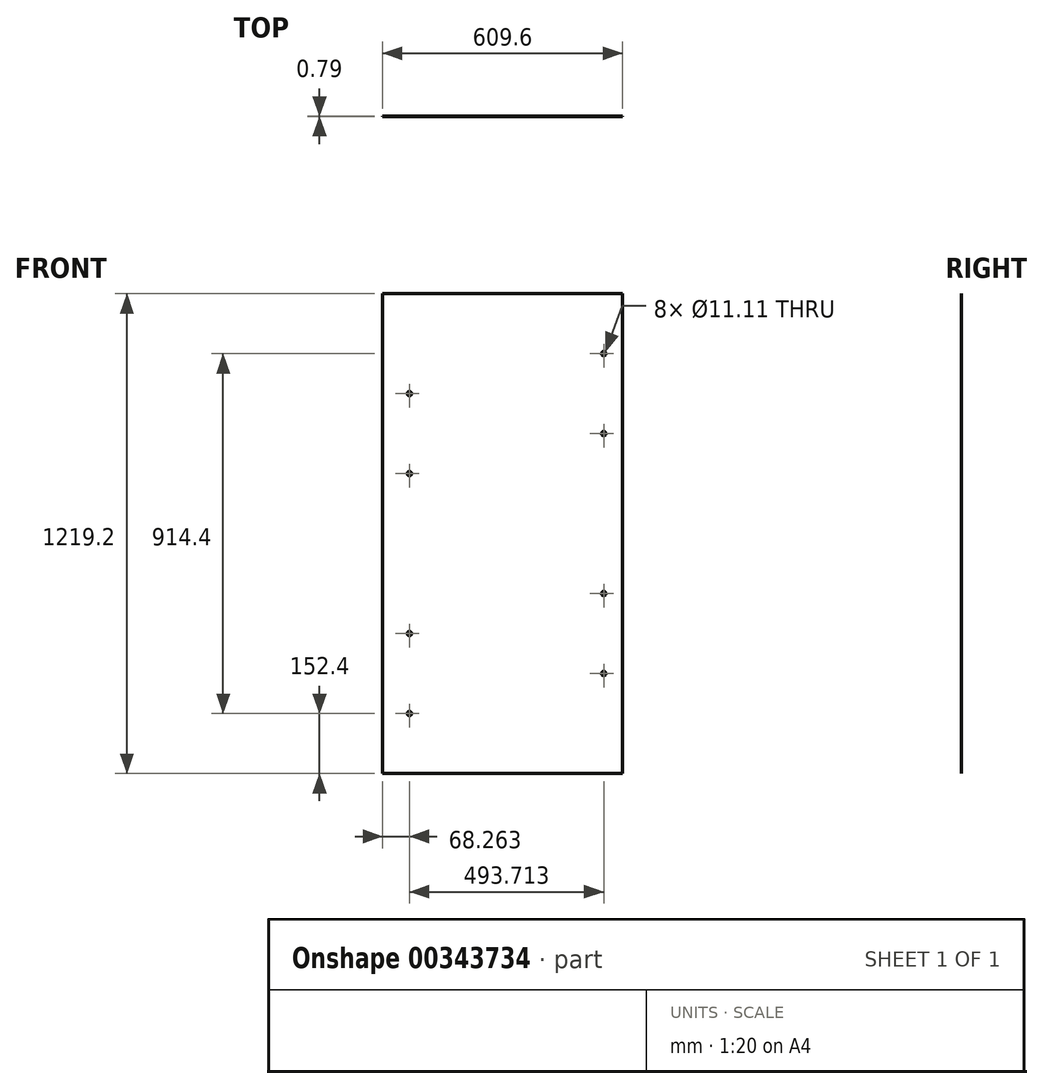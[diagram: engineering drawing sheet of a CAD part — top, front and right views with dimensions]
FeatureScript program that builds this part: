
annotation { "Feature Type Name" : "Feature", "Feature Type Description" : "" }
export const myFeature = defineFeature(function(context is Context, id is Id, definition is map)
    precondition{}
    {
        {
            var Q0;
            Q0=qCreatedBy(makeId("Front.planeOp"),FACE);
            var sketch = newSketch(context, id + "F0", { "sketchPlane" : qUnion([Q0])});
            skLineSegment(sketch, "E0.bottom", {"start": v(0, 0) * mm, "end": v(609.6, 0) * mm});
            skLineSegment(sketch, "E0.top", {"start": v(0, 1219.2) * mm, "end": v(609.6, 1219.2) * mm});
            skLineSegment(sketch, "E0.left", {"start": v(0, 0) * mm, "end": v(0, 1219.2) * mm});
            skLineSegment(sketch, "E0.right", {"start": v(609.6, 0) * mm, "end": v(609.6, 1219.2) * mm});
            skSolve(sketch);
        }
        {
            var Q0;
            Q0=makeQuery(id+"F0.imprint","IMPRINT",FACE,{"disambiguationData":[TD([[makeQuery(id+"F0.imprint","IMPRINT",EDGE,{"derivedFrom":sQuery(id+"F0.wireOp",EDGE,"E0.bottom")}),1.0]])]});
            extrude(context, id + "F1", {"entities" : qUnion([Q0]), "depth" : 0.8 * mm});
        }
        {
            var Q0;
            Q0=makeQuery(id+"F1.opExtrude","CAP_FACE",FACE,{"disambiguationData":[OSD([sQuery(id+"F0.wireOp",EDGE,"E0.bottom"),sQuery(id+"F0.wireOp",EDGE,"E0.top"),sQuery(id+"F0.wireOp",EDGE,"E0.left"),sQuery(id+"F0.wireOp",EDGE,"E0.right")])],"isStart":false});
            var sketch = newSketch(context, id + "F2", { "sketchPlane" : qUnion([Q0])});
            skCircle(sketch, "E1", {"center": v(68.26, 152.4) * mm, "radius": 5.56 * mm});
            skCircle(sketch, "E2", {"center": v(68.26, 355.6) * mm, "radius": 5.56 * mm});
            skCircle(sketch, "E3", {"center": v(561.97, 1066.8) * mm, "radius": 5.56 * mm});
            skCircle(sketch, "E4", {"center": v(561.97, 863.6) * mm, "radius": 5.56 * mm});
            skLineSegment(sketch, "E5", {"start": v(0, 609.6) * mm, "end": v(609.6, 609.6) * mm, "construction": true});
            skCircle(sketch, "E6", {"center": v(68.26, 762) * mm, "radius": 5.56 * mm});
            skCircle(sketch, "E7", {"center": v(68.26, 965.2) * mm, "radius": 5.56 * mm});
            skCircle(sketch, "E8", {"center": v(561.97, 457.2) * mm, "radius": 5.56 * mm});
            skCircle(sketch, "E9", {"center": v(561.97, 254) * mm, "radius": 5.56 * mm});
            skSolve(sketch);
        }
        {
            var Q0;
            Q0=makeQuery(id+"F2.imprint","IMPRINT",FACE,{"disambiguationData":[TD([[makeQuery(id+"F2.imprint","IMPRINT",EDGE,{"derivedFrom":sQuery(id+"F2.wireOp",EDGE,"E1")}),1.0]])]});
            var Q1;
            Q1=makeQuery(id+"F2.imprint","IMPRINT",FACE,{"disambiguationData":[TD([[makeQuery(id+"F2.imprint","IMPRINT",EDGE,{"derivedFrom":sQuery(id+"F2.wireOp",EDGE,"E2")}),1.0]])]});
            var Q2;
            Q2=makeQuery(id+"F2.imprint","IMPRINT",FACE,{"disambiguationData":[TD([[makeQuery(id+"F2.imprint","IMPRINT",EDGE,{"derivedFrom":sQuery(id+"F2.wireOp",EDGE,"E4")}),1.0]])]});
            var Q3;
            Q3=makeQuery(id+"F2.imprint","IMPRINT",FACE,{"disambiguationData":[TD([[makeQuery(id+"F2.imprint","IMPRINT",EDGE,{"derivedFrom":sQuery(id+"F2.wireOp",EDGE,"E3")}),1.0]])]});
            var Q4;
            Q4=makeQuery(id+"F2.imprint","IMPRINT",FACE,{"disambiguationData":[TD([[makeQuery(id+"F2.imprint","IMPRINT",EDGE,{"derivedFrom":sQuery(id+"F2.wireOp",EDGE,"E6")}),1.0]])]});
            var Q5;
            Q5=makeQuery(id+"F2.imprint","IMPRINT",FACE,{"disambiguationData":[TD([[makeQuery(id+"F2.imprint","IMPRINT",EDGE,{"derivedFrom":sQuery(id+"F2.wireOp",EDGE,"E7")}),1.0]])]});
            var Q6;
            Q6=makeQuery(id+"F2.imprint","IMPRINT",FACE,{"disambiguationData":[TD([[makeQuery(id+"F2.imprint","IMPRINT",EDGE,{"derivedFrom":sQuery(id+"F2.wireOp",EDGE,"E9")}),1.0]])]});
            var Q7;
            Q7=makeQuery(id+"F2.imprint","IMPRINT",FACE,{"disambiguationData":[TD([[makeQuery(id+"F2.imprint","IMPRINT",EDGE,{"derivedFrom":sQuery(id+"F2.wireOp",EDGE,"E8")}),1.0]])]});
            extrude(context, id + "F3", {"entities" : qUnion([Q0, Q1, Q2, Q3, Q4, Q5, Q6, Q7]), "operationType" : NewBodyOperationType.REMOVE, "oppositeDirection" : true, "depth" : 25.4 * mm});
        }
    });
